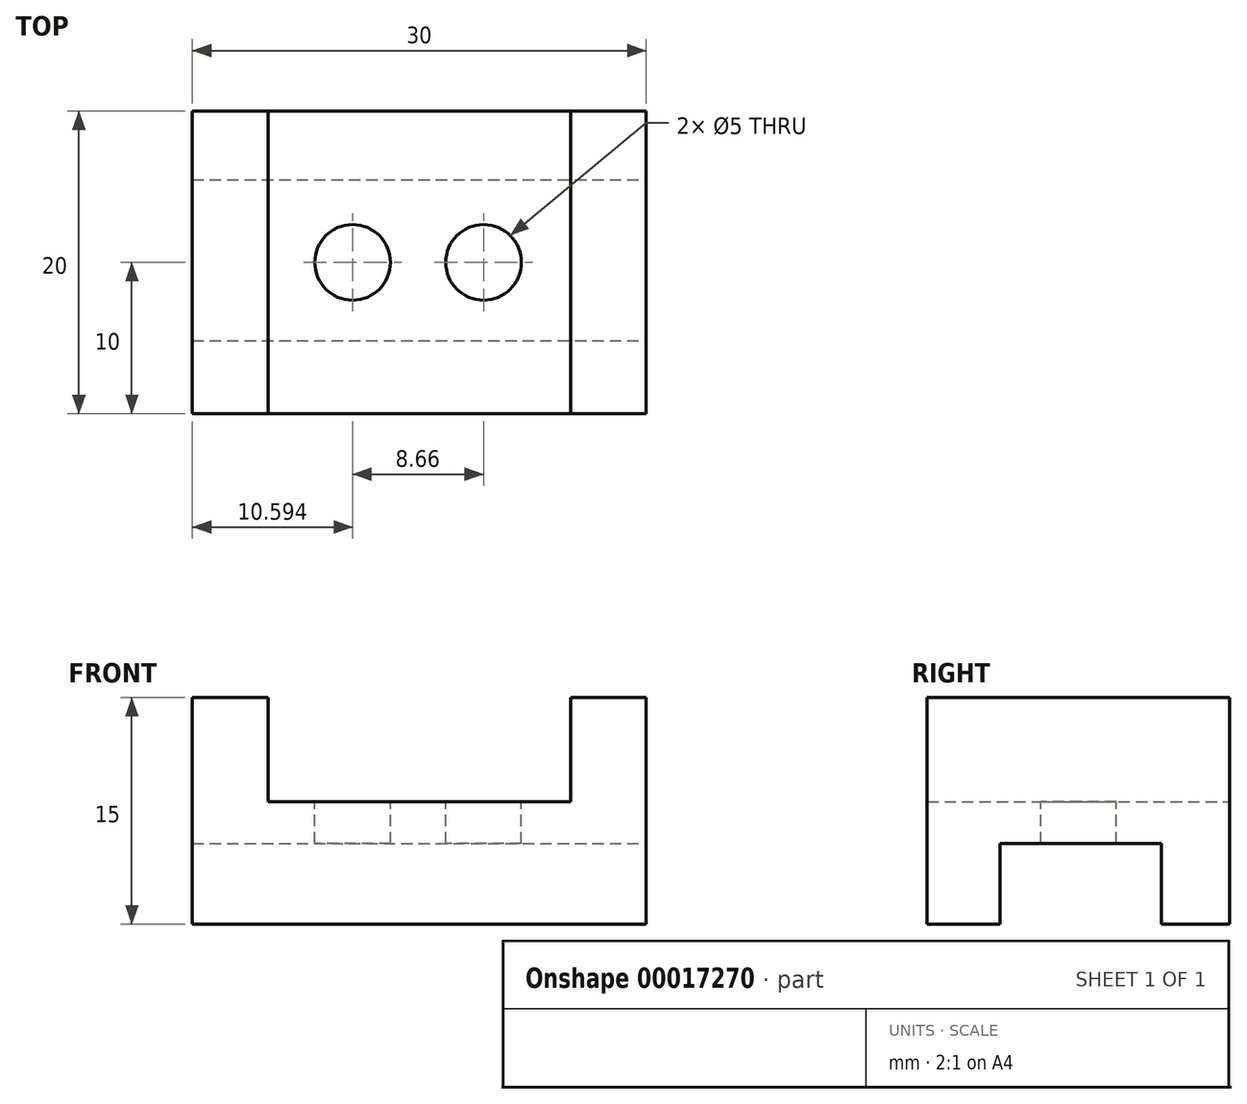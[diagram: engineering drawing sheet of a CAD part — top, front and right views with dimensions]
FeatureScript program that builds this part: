
annotation { "Feature Type Name" : "Feature", "Feature Type Description" : "" }
export const myFeature = defineFeature(function(context is Context, id is Id, definition is map)
    precondition{}
    {
        {
            var Q0;
            Q0=qCreatedBy(makeId("Front.planeOp"),FACE);
            var sketch = newSketch(context, id + "F0", { "sketchPlane" : qUnion([Q0])});
            skLineSegment(sketch, "E0", {"start": v(0, 0) * mm, "end": v(-10, 0) * mm});
            skLineSegment(sketch, "E1", {"start": v(0, 0) * mm, "end": v(10, 0) * mm});
            skLineSegment(sketch, "E2", {"start": v(-10, 0) * mm, "end": v(-10, 6.9) * mm});
            skLineSegment(sketch, "E3", {"start": v(-10, 6.9) * mm, "end": v(-15, 6.9) * mm});
            skLineSegment(sketch, "E4", {"start": v(-15, -8.1) * mm, "end": v(-15, 6.9) * mm});
            skLineSegment(sketch, "E5", {"start": v(10, 0) * mm, "end": v(10, 6.9) * mm});
            skLineSegment(sketch, "E6", {"start": v(15, 6.9) * mm, "end": v(15, -8.1) * mm});
            skLineSegment(sketch, "E7", {"start": v(15, -8.1) * mm, "end": v(-15, -8.1) * mm});
            skLineSegment(sketch, "E8", {"start": v(15, 6.9) * mm, "end": v(10, 6.9) * mm});
            skSolve(sketch);
        }
        {
            var Q0;
            Q0 = qSketchRegion(id + "F0", true);
            extrude(context, id + "F1", {"entities" : qUnion([Q0]), "depth" : 20 * mm});
        }
        {
            var Q0;
            Q0=makeQuery(id+"F1.opExtrude","SWEPT_FACE",FACE,{"disambiguationData":[OSD([sQuery(id+"F0.wireOp",EDGE,"E6")])]});
            var sketch = newSketch(context, id + "F2", { "sketchPlane" : qUnion([Q0])});
            skLineSegment(sketch, "E9", {"start": v(-15.18, -8.1) * mm, "end": v(-15.18, -2.76) * mm});
            skLineSegment(sketch, "E10", {"start": v(-4.53, -8.1) * mm, "end": v(-4.53, -2.76) * mm});
            skLineSegment(sketch, "E11", {"start": v(-4.53, -2.76) * mm, "end": v(-15.18, -2.76) * mm});
            skLineSegment(sketch, "E12", {"start": v(-15.18, -8.1) * mm, "end": v(-4.53, -8.1) * mm});
            skSolve(sketch);
        }
        {
            var Q0;
            Q0 = qSketchRegion(id + "F2", true);
            extrude(context, id + "F3", {"entities" : qUnion([Q0]), "operationType" : NewBodyOperationType.REMOVE, "endBound" : BoundingType.THROUGH_ALL, "oppositeDirection" : true, "depth" : 25 * mm});
        }
        {
            var Q0;
            Q0=makeQuery(id+"F1.opExtrude","SWEPT_FACE",FACE,{"disambiguationData":[OSD([sQuery(id+"F0.wireOp",EDGE,"E0"),sQuery(id+"F0.wireOp",EDGE,"E1")])]});
            var sketch = newSketch(context, id + "F4", { "sketchPlane" : qUnion([Q0])});
            skCircle(sketch, "E13", {"center": v(-4.4, -10) * mm, "radius": 2.5 * mm});
            skCircle(sketch, "E14", {"center": v(4.25, -10) * mm, "radius": 2.5 * mm});
            skSolve(sketch);
        }
        {
            var Q0;
            Q0 = qSketchRegion(id + "F4", true);
            extrude(context, id + "F5", {"entities" : qUnion([Q0]), "operationType" : NewBodyOperationType.REMOVE, "endBound" : BoundingType.THROUGH_ALL, "oppositeDirection" : true, "depth" : 25 * mm});
        }
    });
